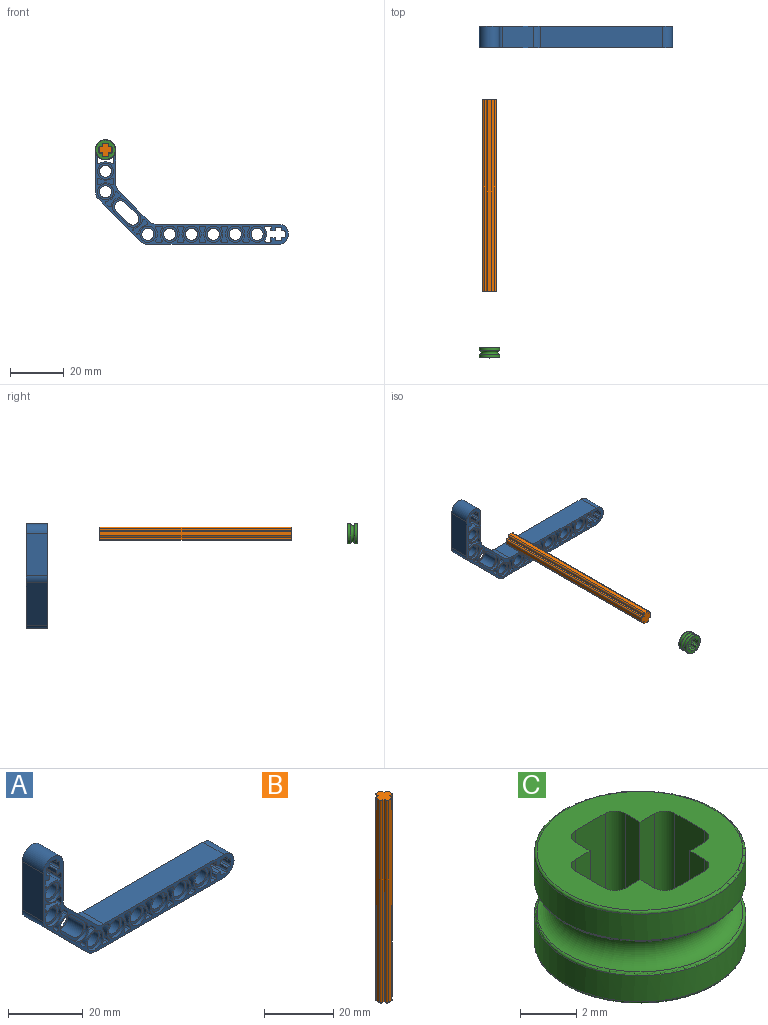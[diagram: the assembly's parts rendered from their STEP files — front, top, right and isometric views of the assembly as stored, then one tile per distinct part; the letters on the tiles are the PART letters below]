
ASSEMBLY  parts=3 mates=2
PART A: 268 faces, bbox 72x8x39 mm
  f0: plane 2.5x1.11mm, normal (0.71,0,0.71), area 3.9mm2, adj f4,f5,f177,f266
  f1: plane 2.5x1.04mm, normal (-0.71,0,-0.71), area 3.7mm2, adj f6,f7,f177,f266
  f2: cylinder r=4mm len=3.2mm, axis (0,1,0), area 11.8mm2, adj f4,f7,f177,f266
  f3: cylinder r=4mm len=3.14mm, axis (0,1,0), area 11.8mm2, adj f5,f6,f177,f266
  f4: cylinder r=0.5mm len=2.5mm, axis (0,1,0), area 2.7mm2, adj f0,f2,f177,f266
  f5: cylinder r=0.5mm len=2.5mm, axis (0,1,0), area 2.7mm2, adj f0,f3,f177,f266
  f6: cylinder r=0.5mm len=2.5mm, axis (0,1,0), area 2.7mm2, adj f1,f3,f177,f266
  f7: cylinder r=0.5mm len=2.5mm, axis (0,1,0), area 2.7mm2, adj f1,f2,f177,f266
  f8: plane 2.5x1.04mm, normal (-0.71,0,-0.71), area 3.7mm2, adj f12,f13,f177,f264
  f9: plane 2.5x1.11mm, normal (0.71,0,0.71), area 3.9mm2, adj f14,f15,f177,f264
  f10: cylinder r=4mm len=3.2mm, axis (0,1,0), area 11.8mm2, adj f12,f15,f177,f264
  f11: cylinder r=4mm len=3.14mm, axis (0,1,0), area 11.8mm2, adj f13,f14,f177,f264
  f12: cylinder r=0.5mm len=2.5mm, axis (0,1,0), area 2.7mm2, adj f8,f10,f177,f264
  f13: cylinder r=0.5mm len=2.5mm, axis (0,1,0), area 2.7mm2, adj f8,f11,f177,f264
  f14: cylinder r=0.5mm len=2.5mm, axis (0,1,0), area 2.7mm2, adj f9,f11,f177,f264
  f15: cylinder r=0.5mm len=2.5mm, axis (0,1,0), area 2.7mm2, adj f9,f10,f177,f264
  f16: plane 2.5x1.52mm, normal (-1,0,0), area 3.8mm2, adj f20,f21,f177,f262
  f17: plane 2.5x1.52mm, normal (1,0,0), area 3.8mm2, adj f22,f23,f177,f262
  f18: cylinder r=4mm len=4.44mm, axis (0,1,0), area 11.8mm2, adj f20,f23,f177,f262
  f19: cylinder r=4mm len=4.44mm, axis (0,1,0), area 11.8mm2, adj f21,f22,f177,f262
  f20: cylinder r=0.5mm len=2.5mm, axis (0,1,0), area 2.7mm2, adj f16,f18,f177,f262
  f21: cylinder r=0.5mm len=2.5mm, axis (0,1,0), area 2.7mm2, adj f16,f19,f177,f262
  f22: cylinder r=0.5mm len=2.5mm, axis (0,1,0), area 2.7mm2, adj f17,f19,f177,f262
  f23: cylinder r=0.5mm len=2.5mm, axis (0,1,0), area 2.7mm2, adj f17,f18,f177,f262
  f24: plane 2.5x1.52mm, normal (0,0,-1), area 3.8mm2, adj f28,f29,f177,f260
  f25: plane 2.5x1.52mm, normal (0,0,1), area 3.8mm2, adj f30,f31,f177,f260
  f26: cylinder r=4mm len=4.44mm, axis (0,1,0), area 11.8mm2, adj f28,f31,f177,f260
  f27: cylinder r=4mm len=4.44mm, axis (0,1,0), area 11.8mm2, adj f29,f30,f177,f260
  f28: cylinder r=0.5mm len=2.5mm, axis (0,1,0), area 2.7mm2, adj f24,f26,f177,f260
  f29: cylinder r=0.5mm len=2.5mm, axis (0,1,0), area 2.7mm2, adj f24,f27,f177,f260
  f30: cylinder r=0.5mm len=2.5mm, axis (0,1,0), area 2.7mm2, adj f25,f27,f177,f260
  f31: cylinder r=0.5mm len=2.5mm, axis (0,1,0), area 2.7mm2, adj f25,f26,f177,f260
  f32: plane 2.5x1.52mm, normal (0,0,-1), area 3.8mm2, adj f36,f37,f177,f258
  f33: plane 2.5x1.52mm, normal (0,0,1), area 3.8mm2, adj f38,f39,f177,f258
  f34: cylinder r=4mm len=4.44mm, axis (0,1,0), area 11.8mm2, adj f36,f39,f177,f258
  f35: cylinder r=4mm len=4.44mm, axis (0,1,0), area 11.8mm2, adj f37,f38,f177,f258
  f36: cylinder r=0.5mm len=2.5mm, axis (0,1,0), area 2.7mm2, adj f32,f34,f177,f258
  f37: cylinder r=0.5mm len=2.5mm, axis (0,1,0), area 2.7mm2, adj f32,f35,f177,f258
  f38: cylinder r=0.5mm len=2.5mm, axis (0,1,0), area 2.7mm2, adj f33,f35,f177,f258
  f39: cylinder r=0.5mm len=2.5mm, axis (0,1,0), area 2.7mm2, adj f33,f34,f177,f258
  f40: plane 2.5x1.52mm, normal (0,0,-1), area 3.8mm2, adj f44,f45,f177,f256
  f41: plane 2.5x1.52mm, normal (0,0,1), area 3.8mm2, adj f46,f47,f177,f256
  f42: cylinder r=4mm len=4.44mm, axis (0,1,0), area 11.8mm2, adj f44,f47,f177,f256
  f43: cylinder r=4mm len=4.44mm, axis (0,1,0), area 11.8mm2, adj f45,f46,f177,f256
  f44: cylinder r=0.5mm len=2.5mm, axis (0,1,0), area 2.7mm2, adj f40,f42,f177,f256
  f45: cylinder r=0.5mm len=2.5mm, axis (0,1,0), area 2.7mm2, adj f40,f43,f177,f256
  f46: cylinder r=0.5mm len=2.5mm, axis (0,1,0), area 2.7mm2, adj f41,f43,f177,f256
  f47: cylinder r=0.5mm len=2.5mm, axis (0,1,0), area 2.7mm2, adj f41,f42,f177,f256
  f48: plane 2.5x1.52mm, normal (0,0,-1), area 3.8mm2, adj f52,f53,f177,f254
  f49: plane 2.5x1.52mm, normal (0,0,1), area 3.8mm2, adj f54,f55,f177,f254
  f50: cylinder r=4mm len=4.44mm, axis (0,1,0), area 11.8mm2, adj f52,f55,f177,f254
  f51: cylinder r=4mm len=4.44mm, axis (0,1,0), area 11.8mm2, adj f53,f54,f177,f254
  f52: cylinder r=0.5mm len=2.5mm, axis (0,1,0), area 2.7mm2, adj f48,f50,f177,f254
  f53: cylinder r=0.5mm len=2.5mm, axis (0,1,0), area 2.7mm2, adj f48,f51,f177,f254
  f54: cylinder r=0.5mm len=2.5mm, axis (0,1,0), area 2.7mm2, adj f49,f51,f177,f254
  f55: cylinder r=0.5mm len=2.5mm, axis (0,1,0), area 2.7mm2, adj f49,f50,f177,f254
  f56: plane 2.5x1.52mm, normal (0,0,-1), area 3.8mm2, adj f60,f61,f177,f252
  f57: plane 2.5x1.52mm, normal (0,0,1), area 3.8mm2, adj f62,f63,f177,f252
  f58: cylinder r=4mm len=4.44mm, axis (0,1,0), area 11.8mm2, adj f60,f63,f177,f252
  f59: cylinder r=4mm len=4.44mm, axis (0,1,0), area 11.8mm2, adj f61,f62,f177,f252
  f60: cylinder r=0.5mm len=2.5mm, axis (0,1,0), area 2.7mm2, adj f56,f58,f177,f252
  f61: cylinder r=0.5mm len=2.5mm, axis (0,1,0), area 2.7mm2, adj f56,f59,f177,f252
  f62: cylinder r=0.5mm len=2.5mm, axis (0,1,0), area 2.7mm2, adj f57,f59,f177,f252
  f63: cylinder r=0.5mm len=2.5mm, axis (0,1,0), area 2.7mm2, adj f57,f58,f177,f252
  f64: plane 4.6x4.6mm, normal (0.71,0,0.71), area 6.5mm2, adj f66,f67,f177,f207
  f65: plane 4.6x4.6mm, normal (-0.71,0,-0.71), area 6.5mm2, adj f66,f67,f177,f207
  f66: cylinder r=3mm len=5.12mm, axis (0,1,0), area 9.4mm2, adj f64,f65,f177,f207
  f67: cylinder r=3mm len=5.12mm, axis (0,1,0), area 9.4mm2, adj f64,f65,f177,f207
  f68: cylinder r=3mm len=6mm, axis (0,1,0), area 18.8mm2, adj f177,f201
  f69: cylinder r=3mm len=6mm, axis (0,1,0), area 18.8mm2, adj f177,f198
  f70: cylinder r=3mm len=6mm, axis (0,1,0), area 18.8mm2, adj f177,f195
  f71: cylinder r=3mm len=6mm, axis (0,1,0), area 18.8mm2, adj f177,f192
  f72: cylinder r=3mm len=6mm, axis (0,1,0), area 18.8mm2, adj f177,f189
  f73: cylinder r=3mm len=6mm, axis (0,1,0), area 18.8mm2, adj f177,f186
  f74: cylinder r=3mm len=6mm, axis (0,1,0), area 18.8mm2, adj f177,f183
  f75: cylinder r=3mm len=6mm, axis (0,1,0), area 18.8mm2, adj f177,f180
  f76: cylinder r=0.5mm len=8mm, axis (0,1,0), area 6.3mm2, adj f77,f175,f176,f177
  f77: plane 8x0.75mm, normal (0,0,1), area 6mm2, adj f76,f78,f176,f177
  f78: plane 8x0.75mm, normal (-1,0,0), area 6mm2, adj f77,f79,f176,f177
  f79: cylinder r=0.5mm len=8mm, axis (0,1,0), area 6.3mm2, adj f78,f80,f176,f177
  f80: plane 8x1.5mm, normal (0,0,1), area 12mm2, adj f79,f81,f176,f177
  f81: cylinder r=0.5mm len=8mm, axis (0,1,0), area 6.3mm2, adj f80,f82,f176,f177
  f82: plane 8x0.75mm, normal (1,0,0), area 6mm2, adj f81,f83,f176,f177
  f83: plane 8x1.21mm, normal (0,0,1), area 9.7mm2, adj f82,f176,f177,f246
  f84: cylinder r=4mm len=8mm, axis (0,1,0), area 2.1mm2, adj f176,f177,f246,f247
  f85: plane 8x1.52mm, normal (0,0,1), area 12.1mm2, adj f176,f177,f247,f248
  f86: cylinder r=4mm len=8mm, axis (0,1,0), area 37.7mm2, adj f176,f177,f248,f249
  f87: plane 8x1.52mm, normal (0,0,-1), area 12.1mm2, adj f176,f177,f249,f250
  f88: cylinder r=4mm len=8mm, axis (0,1,0), area 2.1mm2, adj f176,f177,f250,f251
  f89: plane 8x1.21mm, normal (0,0,-1), area 9.7mm2, adj f90,f176,f177,f251
  f90: plane 8x0.75mm, normal (1,0,0), area 6mm2, adj f89,f91,f176,f177
  f91: cylinder r=0.5mm len=8mm, axis (0,1,0), area 6.3mm2, adj f90,f92,f176,f177
  f92: plane 8x1.5mm, normal (0,0,-1), area 12mm2, adj f91,f93,f176,f177
  f93: cylinder r=0.5mm len=8mm, axis (0,1,0), area 6.3mm2, adj f92,f94,f176,f177
  f94: plane 8x0.75mm, normal (-1,0,0), area 6mm2, adj f93,f95,f176,f177
  f95: plane 8x0.75mm, normal (0,0,-1), area 6mm2, adj f94,f96,f176,f177
  f96: cylinder r=0.5mm len=8mm, axis (0,1,0), area 6.3mm2, adj f95,f175,f176,f177
  f97: cylinder r=4mm len=4.44mm, axis (0,1,0), area 11.8mm2, adj f176,f242,f245,f253
  f98: plane 2.5x1.52mm, normal (0,0,-1), area 3.8mm2, adj f176,f242,f243,f253
  f99: cylinder r=4mm len=4.44mm, axis (0,1,0), area 11.8mm2, adj f176,f243,f244,f253
  f100: cylinder r=4mm len=4.44mm, axis (0,1,0), area 11.8mm2, adj f176,f238,f241,f255
  f101: plane 2.5x1.52mm, normal (0,0,-1), area 3.8mm2, adj f176,f238,f239,f255
  f102: cylinder r=4mm len=4.44mm, axis (0,1,0), area 11.8mm2, adj f176,f239,f240,f255
  f103: cylinder r=4mm len=4.44mm, axis (0,1,0), area 11.8mm2, adj f176,f234,f237,f257
  f104: plane 2.5x1.52mm, normal (0,0,-1), area 3.8mm2, adj f176,f234,f235,f257
  f105: cylinder r=4mm len=4.44mm, axis (0,1,0), area 11.8mm2, adj f176,f235,f236,f257
  f106: cylinder r=4mm len=4.44mm, axis (0,1,0), area 11.8mm2, adj f176,f230,f233,f259
  f107: plane 2.5x1.52mm, normal (0,0,-1), area 3.8mm2, adj f176,f230,f231,f259
  f108: cylinder r=4mm len=4.44mm, axis (0,1,0), area 11.8mm2, adj f176,f231,f232,f259
  f109: cylinder r=4mm len=4.44mm, axis (0,1,0), area 11.8mm2, adj f176,f226,f229,f261
  f110: plane 2.5x1.52mm, normal (0,0,-1), area 3.8mm2, adj f176,f226,f227,f261
  f111: cylinder r=4mm len=4.44mm, axis (0,1,0), area 11.8mm2, adj f176,f227,f228,f261
  f112: cylinder r=4mm len=4.44mm, axis (0,1,0), area 11.8mm2, adj f176,f222,f225,f263
  f113: plane 2.5x1.52mm, normal (-1,0,0), area 3.8mm2, adj f176,f222,f223,f263
  f114: cylinder r=4mm len=4.44mm, axis (0,1,0), area 11.8mm2, adj f176,f223,f224,f263
  f115: plane 8x1.28mm, normal (-1,0,0), area 10.2mm2, adj f162,f176,f177,f216
  f116: cylinder r=4mm len=8mm, axis (0,1,0), area 2.1mm2, adj f176,f177,f216,f217
  f117: plane 8x1.52mm, normal (-1,0,0), area 12.1mm2, adj f176,f177,f217,f218
  f118: cylinder r=4mm len=8mm, axis (0,1,0), area 37.7mm2, adj f176,f177,f218,f219
  f119: plane 8x1.52mm, normal (1,0,0), area 12.1mm2, adj f176,f177,f219,f220
  f120: cylinder r=4mm len=8mm, axis (0,1,0), area 2.1mm2, adj f176,f177,f220,f221
  f121: plane 8x1.28mm, normal (1,0,0), area 10.2mm2, adj f122,f176,f177,f221
  f122: plane 8x0.75mm, normal (0,0,1), area 6mm2, adj f121,f123,f176,f177
  f123: cylinder r=0.5mm len=8mm, axis (0,1,0), area 6.3mm2, adj f122,f124,f176,f177
  f124: plane 8x1.5mm, normal (1,0,0), area 12mm2, adj f123,f125,f176,f177
  f125: cylinder r=0.5mm len=8mm, axis (0,1,0), area 6.3mm2, adj f124,f126,f176,f177
  f126: plane 8x0.75mm, normal (0,0,-1), area 6mm2, adj f125,f127,f176,f177
  f127: plane 8x0.75mm, normal (1,0,0), area 6mm2, adj f126,f128,f176,f177
  f128: cylinder r=0.5mm len=8mm, axis (0,1,0), area 6.3mm2, adj f127,f129,f176,f177
  f129: plane 8x1.5mm, normal (0,0,-1), area 12mm2, adj f128,f130,f176,f177
  f130: cylinder r=0.5mm len=8mm, axis (0,1,0), area 6.3mm2, adj f129,f131,f176,f177
  f131: plane 8x0.75mm, normal (-1,0,0), area 6mm2, adj f130,f132,f176,f177
  f132: plane 8x0.75mm, normal (0,0,-1), area 6mm2, adj f131,f133,f176,f177
  f133: cylinder r=0.5mm len=8mm, axis (0,1,0), area 6.3mm2, adj f132,f134,f176,f177
  f134: plane 8x1.5mm, normal (-1,0,0), area 12mm2, adj f133,f135,f176,f177
  f135: cylinder r=0.5mm len=8mm, axis (0,1,0), area 6.3mm2, adj f134,f162,f176,f177
  f136: cylinder r=4mm len=3.2mm, axis (0,1,0), area 11.8mm2, adj f176,f212,f215,f265
  f137: plane 2.5x1.04mm, normal (-0.71,0,-0.71), area 3.7mm2, adj f176,f212,f213,f265
  f138: cylinder r=4mm len=3.14mm, axis (0,1,0), area 11.8mm2, adj f176,f213,f214,f265
  f139: cylinder r=4mm len=3.2mm, axis (0,1,0), area 11.8mm2, adj f176,f208,f211,f267
  f140: plane 2.5x1.11mm, normal (0.71,0,0.71), area 3.9mm2, adj f176,f208,f209,f267
  f141: cylinder r=4mm len=3.14mm, axis (0,1,0), area 11.8mm2, adj f176,f209,f210,f267
  f142: cylinder r=3mm len=5.12mm, axis (0,1,0), area 9.4mm2, adj f143,f173,f176,f206
  f143: plane 4.6x4.6mm, normal (0.71,0,0.71), area 6.5mm2, adj f142,f144,f176,f206
  f144: cylinder r=3mm len=5.12mm, axis (0,1,0), area 9.4mm2, adj f143,f173,f176,f206
  f145: plane 48.7x8mm, normal (0,0,-1), area 389.6mm2, adj f146,f174,f176,f177
  f146: cylinder r=3.75mm len=8mm, axis (0,1,0), area 94.2mm2, adj f145,f147,f176,f177
  f147: plane 45.59x8mm, normal (0,0,1), area 364.7mm2, adj f146,f148,f176,f177
  f148: cylinder r=3.75mm len=8mm, axis (0,1,0), area 23.6mm2, adj f147,f149,f176,f177
  f149: plane 11.41x11.41mm, normal (0.71,0,0.71), area 129.1mm2, adj f148,f150,f176,f177
  f150: cylinder r=3.75mm len=8mm, axis (0,1,0), area 23.6mm2, adj f149,f151,f176,f177
  f151: plane 12.59x8mm, normal (1,0,0), area 100.7mm2, adj f150,f152,f176,f177
  f152: cylinder r=3.75mm len=8mm, axis (0,1,0), area 94.2mm2, adj f151,f153,f176,f177
  f153: plane 15.7x8mm, normal (-1,0,0), area 125.6mm2, adj f152,f154,f176,f177
  f154: cylinder r=3.75mm len=8mm, axis (0,1,0), area 23.6mm2, adj f153,f155,f176,f177
  f155: plane 15.8x15.8mm, normal (-0.71,0,-0.71), area 178.8mm2, adj f154,f174,f176,f177
  f156: plane 2.5x1.52mm, normal (0,0,1), area 3.8mm2, adj f176,f244,f245,f253
  f157: plane 2.5x1.52mm, normal (0,0,1), area 3.8mm2, adj f176,f240,f241,f255
  f158: plane 2.5x1.52mm, normal (0,0,1), area 3.8mm2, adj f176,f236,f237,f257
  f159: plane 2.5x1.52mm, normal (0,0,1), area 3.8mm2, adj f176,f232,f233,f259
  f160: plane 2.5x1.52mm, normal (0,0,1), area 3.8mm2, adj f176,f228,f229,f261
  f161: plane 2.5x1.52mm, normal (1,0,0), area 3.8mm2, adj f176,f224,f225,f263
  f162: plane 8x0.75mm, normal (0,0,1), area 6mm2, adj f115,f135,f176,f177
  f163: plane 2.5x1.11mm, normal (0.71,0,0.71), area 3.9mm2, adj f176,f214,f215,f265
  f164: plane 2.5x1.04mm, normal (-0.71,0,-0.71), area 3.7mm2, adj f176,f210,f211,f267
  f165: cylinder r=3mm len=6mm, axis (0,1,0), area 18.8mm2, adj f176,f200
  f166: cylinder r=3mm len=6mm, axis (0,1,0), area 18.8mm2, adj f176,f197
  f167: cylinder r=3mm len=6mm, axis (0,1,0), area 18.8mm2, adj f176,f194
  f168: cylinder r=3mm len=6mm, axis (0,1,0), area 18.8mm2, adj f176,f191
  f169: cylinder r=3mm len=6mm, axis (0,1,0), area 18.8mm2, adj f176,f188
  f170: cylinder r=3mm len=6mm, axis (0,1,0), area 18.8mm2, adj f176,f185
  f171: cylinder r=3mm len=6mm, axis (0,1,0), area 18.8mm2, adj f176,f182
  f172: cylinder r=3mm len=6mm, axis (0,1,0), area 18.8mm2, adj f176,f179
  f173: plane 4.6x4.6mm, normal (-0.71,0,-0.71), area 6.5mm2, adj f142,f144,f176,f206
  f174: cylinder r=3.75mm len=8mm, axis (0,1,0), area 23.6mm2, adj f145,f155,f176,f177
  f175: plane 8x1.5mm, normal (-1,0,0), area 12mm2, adj f76,f96,f176,f177
  f176: plane 72x39mm, normal (0,-1,0), area 258.9mm2, adj f76,f77,f78,f79,f80,f81,f82,f83
  f177: plane 72x39mm, normal (0,1,0), area 258.9mm2, adj f0,f1,f2,f3,f4,f5,f6,f7
  f178: cylinder r=2.25mm len=6mm, axis (0,1,0), area 84.8mm2, adj f179,f180
  f179: plane 6x6mm, normal (0,-1,0), area 12.4mm2, adj f172,f178
  f180: plane 6x6mm, normal (0,1,0), area 12.4mm2, adj f75,f178
  f181: cylinder r=2.25mm len=6mm, axis (0,1,0), area 84.8mm2, adj f182,f183
  f182: plane 6x6mm, normal (0,-1,0), area 12.4mm2, adj f171,f181
  f183: plane 6x6mm, normal (0,1,0), area 12.4mm2, adj f74,f181
  f184: cylinder r=2.25mm len=6mm, axis (0,1,0), area 84.8mm2, adj f185,f186
  f185: plane 6x6mm, normal (0,-1,0), area 12.4mm2, adj f170,f184
  f186: plane 6x6mm, normal (0,1,0), area 12.4mm2, adj f73,f184
  f187: cylinder r=2.25mm len=6mm, axis (0,1,0), area 84.8mm2, adj f188,f189
  f188: plane 6x6mm, normal (0,-1,0), area 12.4mm2, adj f169,f187
  f189: plane 6x6mm, normal (0,1,0), area 12.4mm2, adj f72,f187
  f190: cylinder r=2.25mm len=6mm, axis (0,1,0), area 84.8mm2, adj f191,f192
  f191: plane 6x6mm, normal (0,-1,0), area 12.4mm2, adj f168,f190
  f192: plane 6x6mm, normal (0,1,0), area 12.4mm2, adj f71,f190
  f193: cylinder r=2.25mm len=6mm, axis (0,1,0), area 84.8mm2, adj f194,f195
  f194: plane 6x6mm, normal (0,-1,0), area 12.4mm2, adj f167,f193
  f195: plane 6x6mm, normal (0,1,0), area 12.4mm2, adj f70,f193
  f196: cylinder r=2.25mm len=6mm, axis (0,1,0), area 84.8mm2, adj f197,f198
  f197: plane 6x6mm, normal (0,-1,0), area 12.4mm2, adj f166,f196
  f198: plane 6x6mm, normal (0,1,0), area 12.4mm2, adj f69,f196
  f199: cylinder r=2.25mm len=6mm, axis (0,1,0), area 84.8mm2, adj f200,f201
  f200: plane 6x6mm, normal (0,-1,0), area 12.4mm2, adj f165,f199
  f201: plane 6x6mm, normal (0,1,0), area 12.4mm2, adj f68,f199
  f202: cylinder r=2.25mm len=6mm, axis (0,1,0), area 42.4mm2, adj f203,f205,f206,f207
  f203: plane 6x4.6mm, normal (-0.71,0,-0.71), area 39mm2, adj f202,f204,f206,f207
  f204: cylinder r=2.25mm len=6mm, axis (0,1,0), area 42.4mm2, adj f203,f205,f206,f207
  f205: plane 6x4.6mm, normal (0.71,0,0.71), area 39mm2, adj f202,f204,f206,f207
  f206: plane 10.6x10.6mm, normal (0,-1,0), area 22.1mm2, adj f142,f143,f144,f173,f202,f203,f204,f205
  f207: plane 10.6x10.6mm, normal (0,1,0), area 22.1mm2, adj f64,f65,f66,f67,f202,f203,f204,f205
  f208: cylinder r=0.5mm len=2.5mm, axis (0,1,0), area 2.7mm2, adj f139,f140,f176,f267
  f209: cylinder r=0.5mm len=2.5mm, axis (0,1,0), area 2.7mm2, adj f140,f141,f176,f267
  f210: cylinder r=0.5mm len=2.5mm, axis (0,1,0), area 2.7mm2, adj f141,f164,f176,f267
  f211: cylinder r=0.5mm len=2.5mm, axis (0,1,0), area 2.7mm2, adj f139,f164,f176,f267
  f212: cylinder r=0.5mm len=2.5mm, axis (0,1,0), area 2.7mm2, adj f136,f137,f176,f265
  f213: cylinder r=0.5mm len=2.5mm, axis (0,1,0), area 2.7mm2, adj f137,f138,f176,f265
  f214: cylinder r=0.5mm len=2.5mm, axis (0,1,0), area 2.7mm2, adj f138,f163,f176,f265
  f215: cylinder r=0.5mm len=2.5mm, axis (0,1,0), area 2.7mm2, adj f136,f163,f176,f265
  f216: cylinder r=0.5mm len=8mm, axis (0,1,0), area 8.4mm2, adj f115,f116,f176,f177
  f217: cylinder r=0.5mm len=8mm, axis (0,1,0), area 8.6mm2, adj f116,f117,f176,f177
  f218: cylinder r=0.5mm len=8mm, axis (0,1,0), area 8.6mm2, adj f117,f118,f176,f177
  f219: cylinder r=0.5mm len=8mm, axis (0,1,0), area 8.6mm2, adj f118,f119,f176,f177
  f220: cylinder r=0.5mm len=8mm, axis (0,1,0), area 8.6mm2, adj f119,f120,f176,f177
  f221: cylinder r=0.5mm len=8mm, axis (0,1,0), area 8.4mm2, adj f120,f121,f176,f177
  f222: cylinder r=0.5mm len=2.5mm, axis (0,1,0), area 2.7mm2, adj f112,f113,f176,f263
  f223: cylinder r=0.5mm len=2.5mm, axis (0,1,0), area 2.7mm2, adj f113,f114,f176,f263
  f224: cylinder r=0.5mm len=2.5mm, axis (0,1,0), area 2.7mm2, adj f114,f161,f176,f263
  f225: cylinder r=0.5mm len=2.5mm, axis (0,1,0), area 2.7mm2, adj f112,f161,f176,f263
  f226: cylinder r=0.5mm len=2.5mm, axis (0,1,0), area 2.7mm2, adj f109,f110,f176,f261
  f227: cylinder r=0.5mm len=2.5mm, axis (0,1,0), area 2.7mm2, adj f110,f111,f176,f261
  f228: cylinder r=0.5mm len=2.5mm, axis (0,1,0), area 2.7mm2, adj f111,f160,f176,f261
  f229: cylinder r=0.5mm len=2.5mm, axis (0,1,0), area 2.7mm2, adj f109,f160,f176,f261
  f230: cylinder r=0.5mm len=2.5mm, axis (0,1,0), area 2.7mm2, adj f106,f107,f176,f259
  f231: cylinder r=0.5mm len=2.5mm, axis (0,1,0), area 2.7mm2, adj f107,f108,f176,f259
  f232: cylinder r=0.5mm len=2.5mm, axis (0,1,0), area 2.7mm2, adj f108,f159,f176,f259
  f233: cylinder r=0.5mm len=2.5mm, axis (0,1,0), area 2.7mm2, adj f106,f159,f176,f259
  f234: cylinder r=0.5mm len=2.5mm, axis (0,1,0), area 2.7mm2, adj f103,f104,f176,f257
  f235: cylinder r=0.5mm len=2.5mm, axis (0,1,0), area 2.7mm2, adj f104,f105,f176,f257
  f236: cylinder r=0.5mm len=2.5mm, axis (0,1,0), area 2.7mm2, adj f105,f158,f176,f257
  f237: cylinder r=0.5mm len=2.5mm, axis (0,1,0), area 2.7mm2, adj f103,f158,f176,f257
  f238: cylinder r=0.5mm len=2.5mm, axis (0,1,0), area 2.7mm2, adj f100,f101,f176,f255
  f239: cylinder r=0.5mm len=2.5mm, axis (0,1,0), area 2.7mm2, adj f101,f102,f176,f255
  f240: cylinder r=0.5mm len=2.5mm, axis (0,1,0), area 2.7mm2, adj f102,f157,f176,f255
  f241: cylinder r=0.5mm len=2.5mm, axis (0,1,0), area 2.7mm2, adj f100,f157,f176,f255
  f242: cylinder r=0.5mm len=2.5mm, axis (0,1,0), area 2.7mm2, adj f97,f98,f176,f253
  f243: cylinder r=0.5mm len=2.5mm, axis (0,1,0), area 2.7mm2, adj f98,f99,f176,f253
  f244: cylinder r=0.5mm len=2.5mm, axis (0,1,0), area 2.7mm2, adj f99,f156,f176,f253
  f245: cylinder r=0.5mm len=2.5mm, axis (0,1,0), area 2.7mm2, adj f97,f156,f176,f253
  f246: cylinder r=0.5mm len=8mm, axis (0,1,0), area 8.4mm2, adj f83,f84,f176,f177
  f247: cylinder r=0.5mm len=8mm, axis (0,1,0), area 8.6mm2, adj f84,f85,f176,f177
  f248: cylinder r=0.5mm len=8mm, axis (0,1,0), area 8.6mm2, adj f85,f86,f176,f177
  f249: cylinder r=0.5mm len=8mm, axis (0,1,0), area 8.6mm2, adj f86,f87,f176,f177
  f250: cylinder r=0.5mm len=8mm, axis (0,1,0), area 8.6mm2, adj f87,f88,f176,f177
  f251: cylinder r=0.5mm len=8mm, axis (0,1,0), area 8.4mm2, adj f88,f89,f176,f177
  f252: plane 6x2.52mm, normal (0,1,0), area 10mm2, adj f56,f57,f58,f59,f60,f61,f62,f63
  f253: plane 6x2.52mm, normal (0,-1,0), area 10mm2, adj f97,f98,f99,f156,f242,f243,f244,f245
  f254: plane 6x2.52mm, normal (0,1,0), area 10mm2, adj f48,f49,f50,f51,f52,f53,f54,f55
  f255: plane 6x2.52mm, normal (0,-1,0), area 10mm2, adj f100,f101,f102,f157,f238,f239,f240,f241
  f256: plane 6x2.52mm, normal (0,1,0), area 10mm2, adj f40,f41,f42,f43,f44,f45,f46,f47
  f257: plane 6x2.52mm, normal (0,-1,0), area 10mm2, adj f103,f104,f105,f158,f234,f235,f236,f237
  f258: plane 6x2.52mm, normal (0,1,0), area 10mm2, adj f32,f33,f34,f35,f36,f37,f38,f39
  f259: plane 6x2.52mm, normal (0,-1,0), area 10mm2, adj f106,f107,f108,f159,f230,f231,f232,f233
  f260: plane 6x2.52mm, normal (0,1,0), area 10mm2, adj f24,f25,f26,f27,f28,f29,f30,f31
  f261: plane 6x2.52mm, normal (0,-1,0), area 10mm2, adj f109,f110,f111,f160,f226,f227,f228,f229
  f262: plane 6x2.52mm, normal (0,1,0), area 10mm2, adj f16,f17,f18,f19,f20,f21,f22,f23
  f263: plane 6x2.52mm, normal (0,-1,0), area 10mm2, adj f112,f113,f114,f161,f222,f223,f224,f225
  f264: plane 5.64x5.58mm, normal (0,1,0), area 10mm2, adj f8,f9,f10,f11,f12,f13,f14,f15
  f265: plane 5.64x5.58mm, normal (0,-1,0), area 10mm2, adj f136,f137,f138,f163,f212,f213,f214,f215
  f266: plane 5.64x5.58mm, normal (0,1,0), area 10mm2, adj f0,f1,f2,f3,f4,f5,f6,f7
  f267: plane 5.64x5.58mm, normal (0,-1,0), area 10mm2, adj f139,f140,f141,f164,f208,f209,f210,f211
PART B: 62 faces, bbox 5.1x5.1x71.5 mm
  f0: plane 71.3x1.5mm, normal (0,-1,0), area 107mm2, adj f14,f15,f39,f60
  f1: plane 71.3x0.75mm, normal (1,0,0), area 53.5mm2, adj f2,f14,f40,f59
  f2: plane 71.3x0.75mm, normal (0,-1,0), area 53.5mm2, adj f1,f18,f38,f57
  f3: plane 71.3x1.5mm, normal (1,0,0), area 107mm2, adj f18,f19,f34,f53
  f4: plane 71.3x0.75mm, normal (0,1,0), area 53.5mm2, adj f5,f19,f30,f49
  f5: plane 71.3x0.75mm, normal (1,0,0), area 53.5mm2, adj f4,f16,f28,f47
  f6: plane 71.3x1.5mm, normal (0,1,0), area 107mm2, adj f16,f17,f24,f43
  f7: plane 71.3x0.75mm, normal (-1,0,0), area 53.5mm2, adj f8,f17,f23,f44
  f8: plane 71.3x0.75mm, normal (0,1,0), area 53.5mm2, adj f7,f20,f25,f46
  f9: plane 71.3x1.5mm, normal (-1,0,0), area 107mm2, adj f20,f21,f29,f50
  f10: plane 71.3x0.75mm, normal (0,-1,0), area 53.5mm2, adj f11,f21,f33,f54
  f11: plane 71.3x0.75mm, normal (-1,0,0), area 53.5mm2, adj f10,f15,f35,f56
  f12: plane 4.8x4.8mm, normal (0,0,1), area 16.5mm2, adj f22,f23,f24,f25,f26,f27,f28,f29
  f13: plane 4.8x4.8mm, normal (0,0,-1), area 16.5mm2, adj f42,f43,f44,f45,f46,f47,f48,f49
  f14: cylinder r=0.5mm len=71.3mm, axis (0,0,1), area 56mm2, adj f0,f1,f41,f61
  f15: cylinder r=0.5mm len=71.3mm, axis (0,0,-1), area 56mm2, adj f0,f11,f37,f58
  f16: cylinder r=0.5mm len=71.3mm, axis (0,0,-1), area 56mm2, adj f5,f6,f26,f45
  f17: cylinder r=0.5mm len=71.3mm, axis (0,0,1), area 56mm2, adj f6,f7,f22,f42
  f18: cylinder r=0.5mm len=71.3mm, axis (0,0,1), area 56mm2, adj f2,f3,f36,f55
  f19: cylinder r=0.5mm len=71.3mm, axis (0,0,-1), area 56mm2, adj f3,f4,f32,f51
  f20: cylinder r=0.5mm len=71.3mm, axis (0,0,1), area 56mm2, adj f8,f9,f27,f48
  f21: cylinder r=0.5mm len=71.3mm, axis (0,0,-1), area 56mm2, adj f9,f10,f31,f52
  f22: torus R=0.4mm, axis (0,0,1), area 0.1mm2, adj f12,f17,f23,f24
  f23: cylinder r=0.1mm len=0.85mm, axis (0,1,0), area 0.1mm2, adj f7,f12,f22,f25
  f24: cylinder r=0.1mm len=1.5mm, axis (1,0,0), area 0.2mm2, adj f6,f12,f22,f26
  f25: cylinder r=0.1mm len=0.85mm, axis (1,0,0), area 0.1mm2, adj f8,f12,f23,f27
  f26: torus R=0.4mm, axis (0,0,1), area 0.1mm2, adj f12,f16,f24,f28
  f27: torus R=0.4mm, axis (0,0,1), area 0.1mm2, adj f12,f20,f25,f29
  f28: cylinder r=0.1mm len=0.85mm, axis (0,-1,0), area 0.1mm2, adj f5,f12,f26,f30
  f29: cylinder r=0.1mm len=1.5mm, axis (0,1,0), area 0.2mm2, adj f9,f12,f27,f31
  f30: cylinder r=0.1mm len=0.85mm, axis (1,0,0), area 0.1mm2, adj f4,f12,f28,f32
  f31: torus R=0.4mm, axis (0,0,1), area 0.1mm2, adj f12,f21,f29,f33
  f32: torus R=0.4mm, axis (0,0,1), area 0.1mm2, adj f12,f19,f30,f34
  f33: cylinder r=0.1mm len=0.85mm, axis (-1,0,0), area 0.1mm2, adj f10,f12,f31,f35
  f34: cylinder r=0.1mm len=1.5mm, axis (0,-1,0), area 0.2mm2, adj f3,f12,f32,f36
  f35: cylinder r=0.1mm len=0.85mm, axis (0,1,0), area 0.1mm2, adj f11,f12,f33,f37
  f36: torus R=0.4mm, axis (0,0,1), area 0.1mm2, adj f12,f18,f34,f38
  f37: torus R=0.4mm, axis (0,0,1), area 0.1mm2, adj f12,f15,f35,f39
  f38: cylinder r=0.1mm len=0.85mm, axis (-1,0,0), area 0.1mm2, adj f2,f12,f36,f40
  f39: cylinder r=0.1mm len=1.5mm, axis (-1,0,0), area 0.2mm2, adj f0,f12,f37,f41
  f40: cylinder r=0.1mm len=0.85mm, axis (0,-1,0), area 0.1mm2, adj f1,f12,f38,f41
  f41: torus R=0.4mm, axis (0,0,1), area 0.1mm2, adj f12,f14,f39,f40
  f42: torus R=0.4mm, axis (0,0,1), area 0.1mm2, adj f13,f17,f43,f44
  f43: cylinder r=0.1mm len=1.5mm, axis (-1,0,0), area 0.2mm2, adj f6,f13,f42,f45
  f44: cylinder r=0.1mm len=0.85mm, axis (0,-1,0), area 0.1mm2, adj f7,f13,f42,f46
  f45: torus R=0.4mm, axis (0,0,1), area 0.1mm2, adj f13,f16,f43,f47
  f46: cylinder r=0.1mm len=0.85mm, axis (-1,0,0), area 0.1mm2, adj f8,f13,f44,f48
  f47: cylinder r=0.1mm len=0.85mm, axis (0,1,0), area 0.1mm2, adj f5,f13,f45,f49
  f48: torus R=0.4mm, axis (0,0,1), area 0.1mm2, adj f13,f20,f46,f50
  f49: cylinder r=0.1mm len=0.85mm, axis (-1,0,0), area 0.1mm2, adj f4,f13,f47,f51
  f50: cylinder r=0.1mm len=1.5mm, axis (0,-1,0), area 0.2mm2, adj f9,f13,f48,f52
  f51: torus R=0.4mm, axis (0,0,1), area 0.1mm2, adj f13,f19,f49,f53
  f52: torus R=0.4mm, axis (0,0,1), area 0.1mm2, adj f13,f21,f50,f54
  f53: cylinder r=0.1mm len=1.5mm, axis (0,1,0), area 0.2mm2, adj f3,f13,f51,f55
  f54: cylinder r=0.1mm len=0.85mm, axis (1,0,0), area 0.1mm2, adj f10,f13,f52,f56
  f55: torus R=0.4mm, axis (0,0,1), area 0.1mm2, adj f13,f18,f53,f57
  f56: cylinder r=0.1mm len=0.85mm, axis (0,-1,0), area 0.1mm2, adj f11,f13,f54,f58
  f57: cylinder r=0.1mm len=0.85mm, axis (1,0,0), area 0.1mm2, adj f2,f13,f55,f59
  f58: torus R=0.4mm, axis (0,0,1), area 0.1mm2, adj f13,f15,f56,f60
  f59: cylinder r=0.1mm len=0.85mm, axis (0,1,0), area 0.1mm2, adj f1,f13,f57,f61
  f60: cylinder r=0.1mm len=1.5mm, axis (1,0,0), area 0.2mm2, adj f0,f13,f58,f61
  f61: torus R=0.4mm, axis (0,0,1), area 0.1mm2, adj f13,f14,f59,f60
PART C: 29 faces, bbox 8.1x8.1x4 mm
  f0: cylinder r=3.75mm len=7.5mm, axis (0,0,-1), area 26.7mm2, adj f26,f27
  f1: plane 4x0.75mm, normal (-1,0,0), area 3mm2, adj f2,f14,f15,f23
  f2: plane 4x0.75mm, normal (0,-1,0), area 3mm2, adj f1,f14,f15,f16
  f3: plane 4x1.5mm, normal (-1,0,0), area 6mm2, adj f14,f15,f16,f17
  f4: plane 4x0.75mm, normal (0,1,0), area 3mm2, adj f5,f14,f15,f17
  f5: plane 4x0.75mm, normal (-1,0,0), area 3mm2, adj f4,f14,f15,f18
  f6: plane 4x1.5mm, normal (0,1,0), area 6mm2, adj f14,f15,f18,f19
  f7: plane 4x0.75mm, normal (1,0,0), area 3mm2, adj f8,f14,f15,f19
  f8: plane 4x0.75mm, normal (0,1,0), area 3mm2, adj f7,f14,f15,f20
  f9: plane 4x1.5mm, normal (1,0,0), area 6mm2, adj f14,f15,f20,f21
  f10: plane 4x0.75mm, normal (0,-1,0), area 3mm2, adj f11,f14,f15,f21
  f11: plane 4x0.75mm, normal (1,0,0), area 3mm2, adj f10,f14,f15,f22
  f12: cylinder r=3.75mm len=7.5mm, axis (0,0,-1), area 26.7mm2, adj f25,f28
  f13: plane 4x1.5mm, normal (0,-1,0), area 6mm2, adj f14,f15,f22,f23
  f14: plane 7.3x7.3mm, normal (0,0,1), area 23.5mm2, adj f1,f2,f3,f4,f5,f6,f7,f8
  f15: plane 7.3x7.3mm, normal (0,0,-1), area 23.5mm2, adj f1,f2,f3,f4,f5,f6,f7,f8
  f16: cylinder r=0.5mm len=4mm, axis (0,0,-1), area 3.1mm2, adj f2,f3,f14,f15
  f17: cylinder r=0.5mm len=4mm, axis (0,0,1), area 3.1mm2, adj f3,f4,f14,f15
  f18: cylinder r=0.5mm len=4mm, axis (0,0,1), area 3.1mm2, adj f5,f6,f14,f15
  f19: cylinder r=0.5mm len=4mm, axis (0,0,-1), area 3.1mm2, adj f6,f7,f14,f15
  f20: cylinder r=0.5mm len=4mm, axis (0,0,-1), area 3.1mm2, adj f8,f9,f14,f15
  f21: cylinder r=0.5mm len=4mm, axis (0,0,1), area 3.1mm2, adj f9,f10,f14,f15
  f22: cylinder r=0.5mm len=4mm, axis (0,0,1), area 3.1mm2, adj f11,f13,f14,f15
  f23: cylinder r=0.5mm len=4mm, axis (0,0,-1), area 3.1mm2, adj f1,f13,f14,f15
  f24: torus R=3.67mm, axis (0,0,1), area 42mm2, adj f25,f26
  f25: torus R=3.65mm, axis (0,0,-1), area 3.6mm2, adj f12,f24
  f26: torus R=3.65mm, axis (0,0,-1), area 3.6mm2, adj f0,f24
  f27: torus R=3.65mm, axis (0,0,1), area 3.7mm2, adj f0,f15
  f28: torus R=3.65mm, axis (0,0,1), area 3.7mm2, adj f12,f14
PLACE A at identity fixed
PLACE B rot(axis=(1,0,0),90deg) t=(-68.25,-23.45,35.25)mm
PLACE C rot(axis=(1,0,0),90deg) t=(-68.25,-117.77,35.25)mm
MATE slider C.f0 <-> B.f12  axis (0,-1,0) through (-68.25,-119.77,35.25)mm
MATE slider B.f12 <-> A.f152  axis (0,-1,0) through (-68.25,-94.95,35.25)mm
